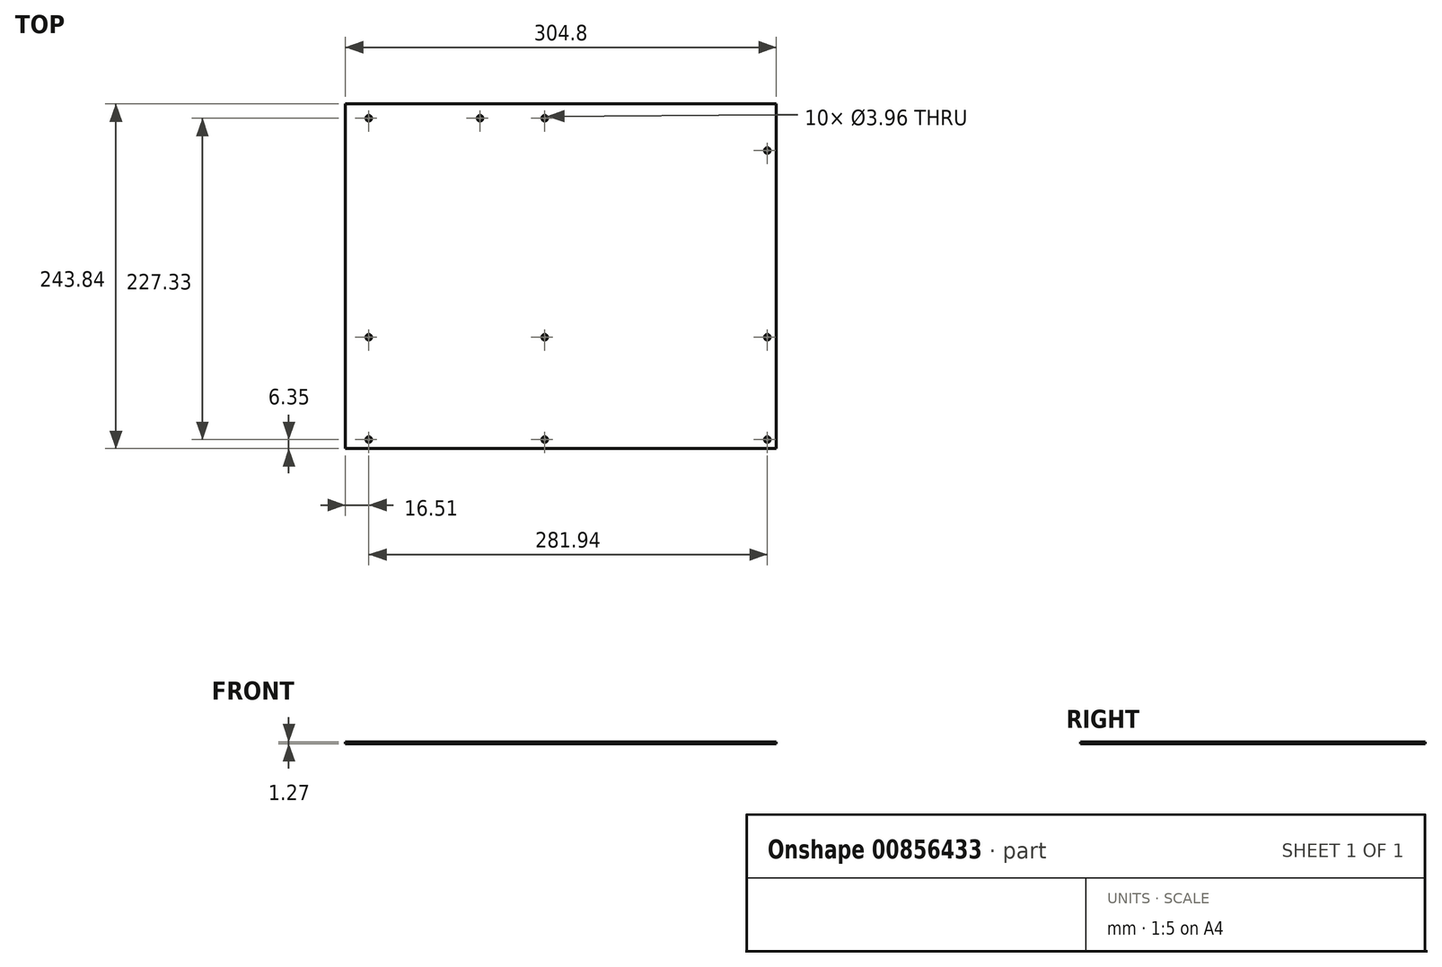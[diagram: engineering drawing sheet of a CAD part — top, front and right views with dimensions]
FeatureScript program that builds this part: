
annotation { "Feature Type Name" : "Feature", "Feature Type Description" : "" }
export const myFeature = defineFeature(function(context is Context, id is Id, definition is map)
    precondition{}
    {
        {
            var Q0;
            Q0=qCreatedBy(makeId("Top.planeOp"),FACE);
            var sketch = newSketch(context, id + "F0", { "sketchPlane" : qUnion([Q0])});
            skLineSegment(sketch, "E0.bottom", {"start": v(-140.97, -78.74) * mm, "end": v(163.83, -78.74) * mm});
            skLineSegment(sketch, "E0.top", {"start": v(-140.97, 165.1) * mm, "end": v(163.83, 165.1) * mm});
            skLineSegment(sketch, "E0.left", {"start": v(-140.97, -78.74) * mm, "end": v(-140.97, 165.1) * mm});
            skLineSegment(sketch, "E0.right", {"start": v(163.83, -78.74) * mm, "end": v(163.83, 165.1) * mm});
            skPoint(sketch, "E1.positionSnap0", {"position": v(163.83, 43.18) * mm});
            skLineSegment(sketch, "E2", {"start": v(0, -181.1) * mm, "end": v(0, 181.1) * mm, "construction": true});
            skCircle(sketch, "E3", {"center": v(-124.46, 154.94) * mm, "radius": 1.98 * mm});
            skLineSegment(sketch, "E4", {"start": v(-124.46, 191.82) * mm, "end": v(-124.46, -176.28) * mm, "construction": true});
            skCircle(sketch, "E5", {"center": v(-124.46, -72.4) * mm, "radius": 1.98 * mm});
            skLineSegment(sketch, "E6", {"start": v(-186.14, -72.4) * mm, "end": v(187.01, -72.4) * mm, "construction": true});
            skCircle(sketch, "E7", {"center": v(0, -72.4) * mm, "radius": 1.98 * mm});
            skCircle(sketch, "E8", {"center": v(157.48, -72.4) * mm, "radius": 1.98 * mm});
            skLineSegment(sketch, "E9", {"start": v(-174.7, 0) * mm, "end": v(198.44, 0) * mm, "construction": true});
            skLineSegment(sketch, "E10", {"start": v(157.48, 191.82) * mm, "end": v(157.48, -176.28) * mm, "construction": true});
            skLineSegment(sketch, "E11", {"start": v(-173, 154.94) * mm, "end": v(94.1, 154.94) * mm, "construction": true});
            skCircle(sketch, "E12", {"center": v(-45.72, 154.94) * mm, "radius": 1.98 * mm});
            skCircle(sketch, "E13", {"center": v(0, 154.94) * mm, "radius": 1.98 * mm});
            skCircle(sketch, "E14", {"center": v(0, 0) * mm, "radius": 1.98 * mm});
            skCircle(sketch, "E15", {"center": v(157.48, 132.08) * mm, "radius": 1.98 * mm});
            skCircle(sketch, "E16", {"center": v(157.48, 0) * mm, "radius": 1.98 * mm});
            skCircle(sketch, "E17", {"center": v(-124.46, 0) * mm, "radius": 1.98 * mm});
            skSolve(sketch);
        }
        {
            var Q0;
            Q0=makeQuery(id+"F0.imprint","IMPRINT",FACE,{"disambiguationData":[TD([[makeQuery(id+"F0.imprint","IMPRINT",EDGE,{"derivedFrom":sQuery(id+"F0.wireOp",EDGE,"E0.bottom")}),1.0]])]});
            extrude(context, id + "F1", {"entities" : qUnion([Q0]), "depth" : 1.27 * mm, "offsetDistance" : 25.4 * mm});
        }
    });
